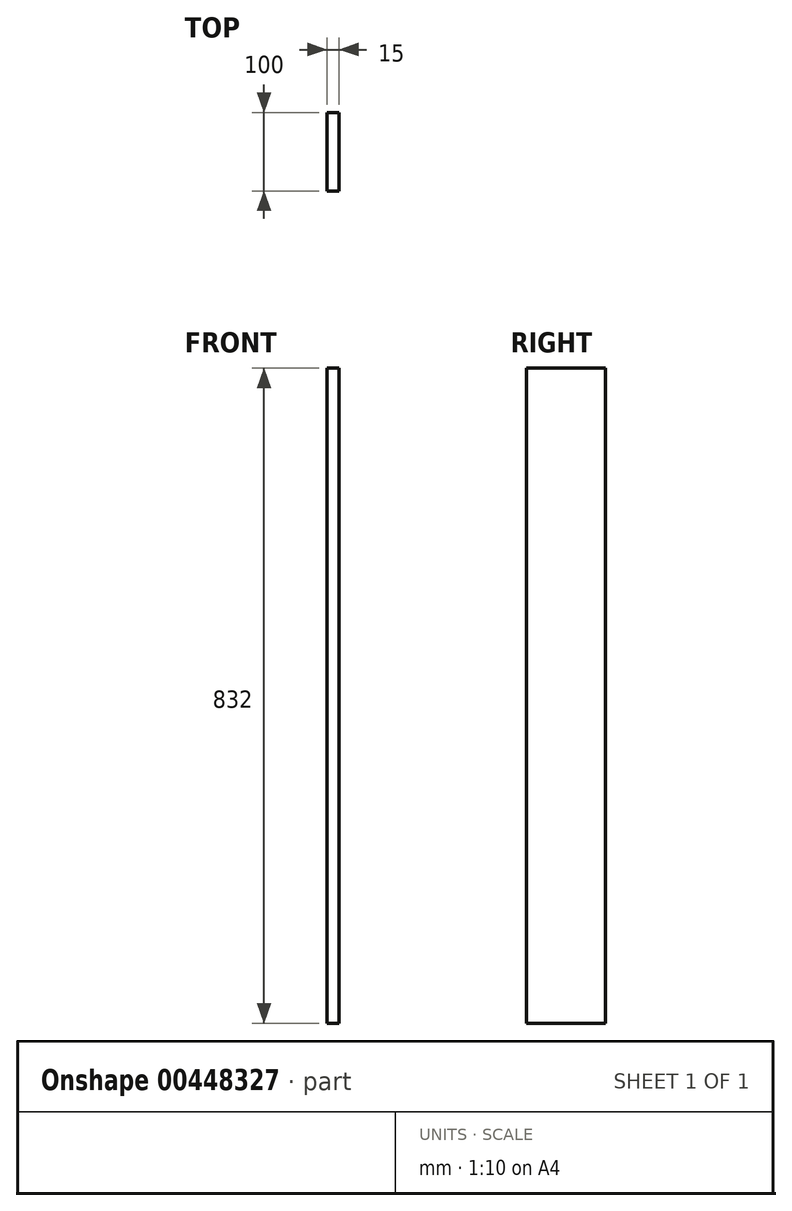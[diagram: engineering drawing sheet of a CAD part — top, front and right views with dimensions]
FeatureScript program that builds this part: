
annotation { "Feature Type Name" : "Feature", "Feature Type Description" : "" }
export const myFeature = defineFeature(function(context is Context, id is Id, definition is map)
    precondition{}
    {
        {
            var Q0;
            Q0=qCreatedBy(makeId("Right.planeOp"),FACE);
            var sketch = newSketch(context, id + "F0", { "sketchPlane" : qUnion([Q0])});
            skLineSegment(sketch, "E0.bottom", {"start": v(0, 0) * mm, "end": v(100, 0) * mm});
            skLineSegment(sketch, "E0.top", {"start": v(0, 832) * mm, "end": v(100, 832) * mm});
            skLineSegment(sketch, "E0.left", {"start": v(0, 0) * mm, "end": v(0, 832) * mm});
            skLineSegment(sketch, "E0.right", {"start": v(100, 0) * mm, "end": v(100, 832) * mm});
            skSolve(sketch);
        }
        {
            var Q0;
            Q0=makeQuery(id+"F0.imprint","IMPRINT",FACE,{"disambiguationData":[TD([[makeQuery(id+"F0.imprint","IMPRINT",EDGE,{"derivedFrom":sQuery(id+"F0.wireOp",EDGE,"E0.bottom")}),1.0]])]});
            extrude(context, id + "F1", {"entities" : qUnion([Q0]), "depth" : 15 * mm});
        }
    });
